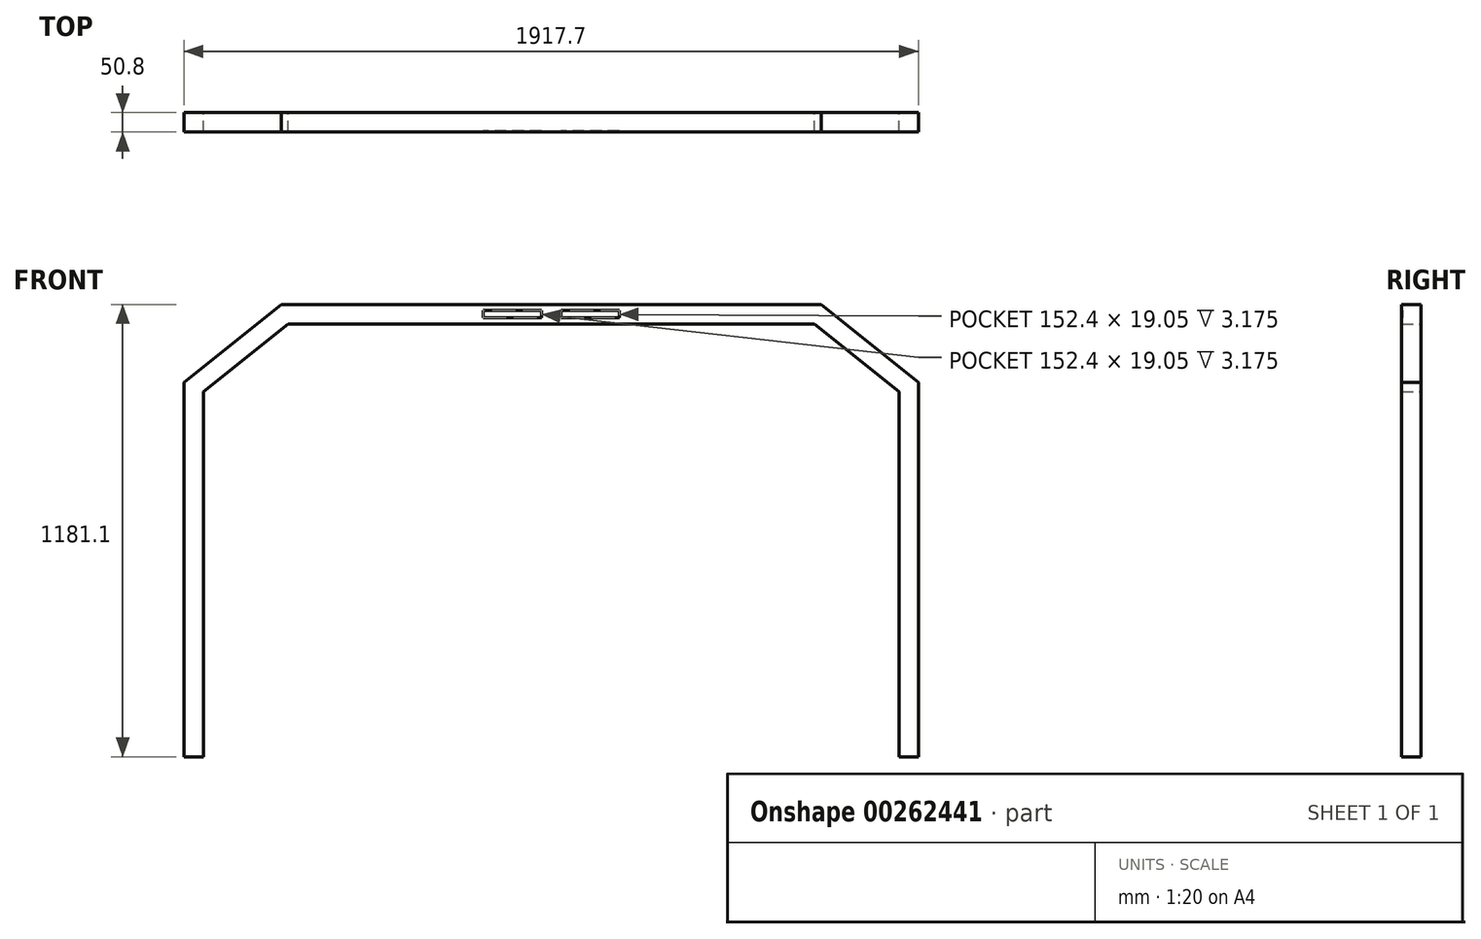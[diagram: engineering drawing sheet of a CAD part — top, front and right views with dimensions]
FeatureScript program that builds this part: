
annotation { "Feature Type Name" : "Feature", "Feature Type Description" : "" }
export const myFeature = defineFeature(function(context is Context, id is Id, definition is map)
    precondition{}
    {
        {
            var Q0;
            Q0=qCreatedBy(makeId("Front.planeOp"),FACE);
            var sketch = newSketch(context, id + "F0", { "sketchPlane" : qUnion([Q0])});
            skLineSegment(sketch, "E0.bottom", {"start": v(704.85, 590.55) * mm, "end": v(-704.85, 590.55) * mm});
            skLineSegment(sketch, "E0.top", {"start": v(958.85, -590.55) * mm, "end": v(908.05, -590.55) * mm});
            skLineSegment(sketch, "E0.left", {"start": v(958.85, 387.35) * mm, "end": v(958.85, -590.55) * mm});
            skLineSegment(sketch, "E0.right", {"start": v(-958.85, 387.35) * mm, "end": v(-958.85, -590.55) * mm});
            skPoint(sketch, "E0.middle", {"position": v(0, 0) * mm});
            skLineSegment(sketch, "E1", {"start": v(-958.85, 387.35) * mm, "end": v(-704.85, 590.55) * mm});
            skLineSegment(sketch, "E2", {"start": v(958.85, 387.35) * mm, "end": v(704.85, 590.55) * mm});
            skLineSegment(sketch, "E3", {"start": v(-908.05, -590.55) * mm, "end": v(-908.05, 362.93) * mm});
            skLineSegment(sketch, "E4", {"start": v(-908.05, 362.93) * mm, "end": v(-687.03, 539.75) * mm});
            skLineSegment(sketch, "E5", {"start": v(-687.03, 539.75) * mm, "end": v(687.03, 539.75) * mm});
            skLineSegment(sketch, "E6", {"start": v(687.03, 539.75) * mm, "end": v(908.05, 362.93) * mm});
            skLineSegment(sketch, "E7", {"start": v(908.05, 362.93) * mm, "end": v(908.05, -590.55) * mm});
            skLineSegment(sketch, "E8.trimOffspring", {"start": v(-908.05, -590.55) * mm, "end": v(-958.85, -590.55) * mm});
            skPoint(sketch, "E9.orphan", {"position": v(-958.85, 590.55) * mm});
            skPoint(sketch, "E10.orphan", {"position": v(958.85, 590.55) * mm});
            skSolve(sketch);
        }
        {
            var Q0;
            Q0 = qSketchRegion(id + "F0", true);
            extrude(context, id + "F1", {"entities" : qUnion([Q0]), "depth" : 50.8 * mm});
        }
        {
            var Q0;
            Q0=makeQuery(id+"F1.opExtrude","CAP_FACE",FACE,{"disambiguationData":[OSD([sQuery(id+"F0.wireOp",EDGE,"E0.bottom"),sQuery(id+"F0.wireOp",EDGE,"E0.top"),sQuery(id+"F0.wireOp",EDGE,"E0.left"),sQuery(id+"F0.wireOp",EDGE,"E0.right"),sQuery(id+"F0.wireOp",EDGE,"E1"),sQuery(id+"F0.wireOp",EDGE,"E2"),sQuery(id+"F0.wireOp",EDGE,"E3"),sQuery(id+"F0.wireOp",EDGE,"E4"),sQuery(id+"F0.wireOp",EDGE,"E5"),sQuery(id+"F0.wireOp",EDGE,"E6"),sQuery(id+"F0.wireOp",EDGE,"E7"),sQuery(id+"F0.wireOp",EDGE,"E8.trimOffspring")])],"isStart":false});
            var sketch = newSketch(context, id + "F2", { "sketchPlane" : qUnion([Q0])});
            skLineSegment(sketch, "E11", {"start": v(-704.85, 590.55) * mm, "end": v(0, 590.55) * mm});
            skLineSegment(sketch, "E12.bottom", {"start": v(-25.4, 555.62) * mm, "end": v(-177.8, 555.62) * mm});
            skLineSegment(sketch, "E12.top", {"start": v(-25.4, 574.68) * mm, "end": v(-177.8, 574.68) * mm});
            skLineSegment(sketch, "E12.left", {"start": v(-25.4, 555.62) * mm, "end": v(-25.4, 574.68) * mm});
            skLineSegment(sketch, "E12.right", {"start": v(-177.8, 555.62) * mm, "end": v(-177.8, 574.68) * mm});
            skPoint(sketch, "E12.middle", {"position": v(-101.6, 565.15) * mm});
            skLineSegment(sketch, "E13.bottom", {"start": v(177.8, 555.62) * mm, "end": v(25.4, 555.62) * mm});
            skLineSegment(sketch, "E13.top", {"start": v(177.8, 574.68) * mm, "end": v(25.4, 574.68) * mm});
            skLineSegment(sketch, "E13.left", {"start": v(177.8, 555.62) * mm, "end": v(177.8, 574.68) * mm});
            skLineSegment(sketch, "E13.right", {"start": v(25.4, 555.62) * mm, "end": v(25.4, 574.68) * mm});
            skPoint(sketch, "E13.middle", {"position": v(101.6, 565.15) * mm});
            skSolve(sketch);
        }
        {
            var Q0;
            Q0 = qSketchRegion(id + "F2", true);
            extrude(context, id + "F3", {"entities" : qUnion([Q0]), "operationType" : NewBodyOperationType.REMOVE, "oppositeDirection" : true, "depth" : 3.17 * mm});
        }
    });
